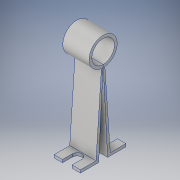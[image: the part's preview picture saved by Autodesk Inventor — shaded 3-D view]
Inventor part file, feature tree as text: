
AUTODESK INVENTOR PART (.ipt)
format: ipt  version: 2018 (Build 220112000, 112)  size: 145,920 bytes
history: native  units: in
note: dims shown in document units (in); Inventor stores cm internally (conversion verified against a paired STEP export)
features: extrude x2, sketch x2
ambient origin geometry x8: Origin, YZ Plane, XZ Plane, XY Plane, X Axis, Y Axis, Z Axis, Center Point
bodies: Solid1 (feature_tree)
feature tree (4):
  extrude  "Extrusion1"  Depth=0.31in
  extrude  "Extrusion2"  Depth=0.115in
  sketch  "Sketch2"  dims[d2=0.385in d3=0.31in]
  sketch  "Sketch3"  dims[d12=0.36in d13=0.0in d14=0.115in d15=0.115in d17=0.36in d18=0.0in]
